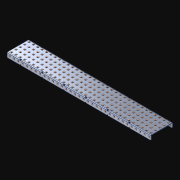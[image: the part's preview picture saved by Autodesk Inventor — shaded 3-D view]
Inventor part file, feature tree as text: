
AUTODESK INVENTOR PART (.ipt)
format: ipt  version: 2021 (Build 250183000, 183)  size: 2,438,656 bytes
history: native  units: in
note: dims shown in document units (in); Inventor stores cm internally (conversion verified against a paired STEP export)
features: extrude x232, other x232, sketch x4, pattern_linear x3
ambient origin geometry x8: Origin, YZ Plane, XZ Plane, XY Plane, X Axis, Y Axis, Z Axis, Center Point
bodies: Solid1 (feature_tree)
feature tree (471):
  pattern_linear  "Rectangular Pattern1"  Spacing1=0.182in  [1 undecoded]
  pattern_linear  "Rectangular Pattern2"  Spacing1=0.046in  [1 undecoded]
  pattern_linear  "Rectangular Pattern3"  Spacing1=0.5in  [1 undecoded]
  extrude  "Extrusion1"  Depth=1.0in
  sketch  "Sketch1"  dims[d0=0.182in]
  other  "Srf1"
  sketch  "Sketch2"  dims[d1=0.046in d2=0.0in]
  other  "Srf2"
  sketch  "Sketch3"  dims[d3=0.182in]
  other  "Srf3"
  other  "Srf4"
  other  "Srf5"
  other  "Srf6"
  other  "Srf7"
  other  "Srf8"
  other  "Srf9"
  other  "Srf10"
  other  "Srf11"
  other  "Srf12"
  other  "Srf13"
  other  "Srf14"
  other  "Srf15"
  other  "Srf16"
  other  "Srf17"
  other  "Srf18"
  other  "Srf19"
  other  "Srf20"
  other  "Srf21"
  other  "Srf22"
  other  "Srf23"
  other  "Srf24"
  other  "Srf25"
  other  "Srf26"
  other  "Srf27"
  other  "Srf28"
  other  "Srf29"
  other  "Srf30"
  other  "Srf31"
  other  "Srf32"
  other  "Srf33"
  other  "Srf34"
  other  "Srf35"
  other  "Srf38"
  other  "Srf39"
  other  "Srf40"
  other  "Srf41"
  other  "Srf42"
  other  "Srf43"
  other  "Srf44"
  other  "Srf45"
  other  "Srf46"
  other  "Srf47"
  other  "Srf48"
  other  "Srf49"
  other  "Srf50"
  other  "Srf51"
  other  "Srf52"
  other  "Srf53"
  other  "Srf54"
  other  "Srf55"
  other  "Srf56"
  other  "Srf57"
  other  "Srf58"
  other  "Srf59"
  other  "Srf60"
  other  "Srf61"
  other  "Srf62"
  other  "Srf63"
  other  "Srf64"
  other  "Srf65"
  other  "Srf66"
  other  "Srf67"
  other  "Srf68"
  other  "Srf69"
  other  "Srf72"
  other  "Srf73"
  other  "Srf74"
  other  "Srf75"
  other  "Srf76"
  other  "Srf77"
  other  "Srf78"
  other  "Srf79"
  other  "Srf80"
  other  "Srf81"
  other  "Srf82"
  other  "Srf83"
  other  "Srf84"
  other  "Srf85"
  other  "Srf86"
  other  "Srf87"
  other  "Srf88"
  other  "Srf89"
  other  "Srf90"
  other  "Srf91"
  other  "Srf92"
  other  "Srf93"
  other  "Srf94"
  other  "Srf95"
  other  "Srf96"
  other  "Srf97"
  other  "Srf98"
  other  "Srf99"
  other  "Srf100"
  other  "Srf101"
  other  "Srf102"
  other  "Srf103"
  other  "Srf104"
  other  "Srf107"
  other  "Srf108"
  other  "Srf109"
  other  "Srf110"
  other  "Srf111"
  other  "Srf112"
  other  "Srf113"
  other  "Srf114"
  other  "Srf115"
  other  "Srf116"
  other  "Srf117"
  other  "Srf118"
  other  "Srf119"
  other  "Srf120"
  other  "Srf121"
  other  "Srf122"
  other  "Srf123"
  other  "Srf124"
  other  "Srf125"
  other  "Srf126"
  other  "Srf127"
  other  "Srf128"
  other  "Srf129"
  other  "Srf130"
  other  "Srf131"
  other  "Srf132"
  other  "Srf133"
  other  "Srf134"
  other  "Srf135"
  other  "Srf136"
  other  "Srf137"
  other  "Srf138"
  other  "Srf139"
  other  "Srf142"
  other  "Srf143"
  other  "Srf144"
  other  "Srf145"
  other  "Srf146"
  other  "Srf147"
  other  "Srf148"
  other  "Srf149"
  other  "Srf150"
  other  "Srf151"
  other  "Srf152"
  other  "Srf153"
  other  "Srf154"
  other  "Srf155"
  other  "Srf156"
  other  "Srf157"
  other  "Srf158"
  other  "Srf159"
  other  "Srf160"
  other  "Srf161"
  other  "Srf162"
  other  "Srf163"
  other  "Srf164"
  other  "Srf165"
  other  "Srf166"
  other  "Srf167"
  other  "Srf168"
  other  "Srf169"
  other  "Srf170"
  other  "Srf171"
  other  "Srf172"
  other  "Srf173"
  other  "Srf174"
  other  "Srf177"
  other  "Srf178"
  other  "Srf179"
  other  "Srf180"
  other  "Srf181"
  other  "Srf182"
  other  "Srf183"
  other  "Srf184"
  other  "Srf185"
  other  "Srf186"
  other  "Srf187"
  other  "Srf188"
  other  "Srf189"
  other  "Srf190"
  other  "Srf191"
  other  "Srf192"
  other  "Srf193"
  other  "Srf194"
  other  "Srf195"
  other  "Srf196"
  other  "Srf197"
  other  "Srf198"
  other  "Srf199"
  other  "Srf200"
  other  "Srf201"
  other  "Srf202"
  other  "Srf203"
  other  "Srf204"
  other  "Srf205"
  other  "Srf206"
  other  "Srf207"
  other  "Srf208"
  other  "Srf209"
  other  "Srf212"
  other  "Srf213"
  other  "Srf214"
  other  "Srf215"
  other  "Srf216"
  other  "Srf217"
  other  "Srf218"
  other  "Srf219"
  other  "Srf220"
  other  "Srf221"
  other  "Srf222"
  other  "Srf223"
  other  "Srf224"
  other  "Srf225"
  other  "Srf226"
  other  "Srf227"
  other  "Srf228"
  other  "Srf229"
  other  "Srf230"
  other  "Srf231"
  other  "Srf232"
  other  "Srf233"
  other  "Srf234"
  other  "Srf235"
  other  "Srf236"
  other  "Srf237"
  other  "Srf238"
  other  "Srf239"
  other  "Srf240"
  other  "Srf241"
  other  "Srf242"
  other  "Srf243"
  sketch  "Sketch4"  dims[d4=0.046in d5=0.0in d6=0.182in d7=0.046in d8=0.0in d11=0.5in d12=12.9921in d14=0.5in d15=1.9685in d17=0.5in d18=12.9921in d20=0.5in d21=1.0in d22=0.0in]
  parser-record x1  (decoder bookkeeping rows leaked as tree rows — omitted from the tree; the rows remain in map.json)
  extrude  "ExtrusionSrf1"  Depth=1.0in
  extrude  "ExtrusionSrf2"  Depth=1.0in
  extrude  "ExtrusionSrf3"  Depth=1.0in
  extrude  "ExtrusionSrf4"  Depth=1.0in
  extrude  "ExtrusionSrf5"  Depth=1.0in
  extrude  "ExtrusionSrf6"  TaperAngle=0.0deg  [1 undecoded]
  extrude  "ExtrusionSrf7"  [1 undecoded]
  extrude  "ExtrusionSrf8"  [1 undecoded]
  extrude  "ExtrusionSrf9"  [1 undecoded]
  extrude  "ExtrusionSrf10"  [1 undecoded]
  extrude  "ExtrusionSrf11"  [1 undecoded]
  extrude  "ExtrusionSrf12"  [1 undecoded]
  extrude  "ExtrusionSrf13"  [1 undecoded]
  extrude  "ExtrusionSrf14"  [1 undecoded]
  extrude  "ExtrusionSrf15"  [1 undecoded]
  extrude  "ExtrusionSrf16"  [1 undecoded]
  extrude  "ExtrusionSrf17"  [1 undecoded]
  extrude  "ExtrusionSrf18"  [1 undecoded]
  extrude  "ExtrusionSrf19"  [1 undecoded]
  extrude  "ExtrusionSrf20"  [1 undecoded]
  extrude  "ExtrusionSrf21"  [1 undecoded]
  extrude  "ExtrusionSrf22"  [1 undecoded]
  extrude  "ExtrusionSrf23"  [1 undecoded]
  extrude  "ExtrusionSrf24"  [1 undecoded]
  extrude  "ExtrusionSrf25"  [1 undecoded]
  extrude  "ExtrusionSrf26"  [1 undecoded]
  extrude  "ExtrusionSrf27"  [1 undecoded]
  extrude  "ExtrusionSrf28"  [1 undecoded]
  extrude  "ExtrusionSrf29"  [1 undecoded]
  extrude  "ExtrusionSrf30"  [1 undecoded]
  extrude  "ExtrusionSrf31"  [1 undecoded]
  extrude  "ExtrusionSrf32"  [1 undecoded]
  extrude  "ExtrusionSrf33"  [1 undecoded]
  extrude  "ExtrusionSrf34"  [1 undecoded]
  extrude  "ExtrusionSrf35"  [1 undecoded]
  extrude  "ExtrusionSrf38"  [1 undecoded]
  extrude  "ExtrusionSrf39"  [1 undecoded]
  extrude  "ExtrusionSrf40"  [1 undecoded]
  extrude  "ExtrusionSrf41"  [1 undecoded]
  extrude  "ExtrusionSrf42"  [1 undecoded]
  extrude  "ExtrusionSrf43"  [1 undecoded]
  extrude  "ExtrusionSrf44"  [1 undecoded]
  extrude  "ExtrusionSrf45"  [1 undecoded]
  extrude  "ExtrusionSrf46"  [1 undecoded]
  extrude  "ExtrusionSrf47"  [1 undecoded]
  extrude  "ExtrusionSrf48"  [1 undecoded]
  extrude  "ExtrusionSrf49"  [1 undecoded]
  extrude  "ExtrusionSrf50"  [1 undecoded]
  extrude  "ExtrusionSrf51"  [1 undecoded]
  extrude  "ExtrusionSrf52"  [1 undecoded]
  extrude  "ExtrusionSrf53"  [1 undecoded]
  extrude  "ExtrusionSrf54"  [1 undecoded]
  extrude  "ExtrusionSrf55"  [1 undecoded]
  extrude  "ExtrusionSrf56"  [1 undecoded]
  extrude  "ExtrusionSrf57"  [1 undecoded]
  extrude  "ExtrusionSrf58"  [1 undecoded]
  extrude  "ExtrusionSrf59"  [1 undecoded]
  extrude  "ExtrusionSrf60"  [1 undecoded]
  extrude  "ExtrusionSrf61"  [1 undecoded]
  extrude  "ExtrusionSrf62"  [1 undecoded]
  extrude  "ExtrusionSrf63"  [1 undecoded]
  extrude  "ExtrusionSrf64"  [1 undecoded]
  extrude  "ExtrusionSrf65"  [1 undecoded]
  extrude  "ExtrusionSrf66"  [1 undecoded]
  extrude  "ExtrusionSrf67"  [1 undecoded]
  extrude  "ExtrusionSrf68"  [1 undecoded]
  extrude  "ExtrusionSrf69"  [1 undecoded]
  extrude  "ExtrusionSrf72"  [1 undecoded]
  extrude  "ExtrusionSrf73"  [1 undecoded]
  extrude  "ExtrusionSrf74"  [1 undecoded]
  extrude  "ExtrusionSrf75"  [1 undecoded]
  extrude  "ExtrusionSrf76"  [1 undecoded]
  extrude  "ExtrusionSrf77"  [1 undecoded]
  extrude  "ExtrusionSrf78"  [1 undecoded]
  extrude  "ExtrusionSrf79"  [1 undecoded]
  extrude  "ExtrusionSrf80"  [1 undecoded]
  extrude  "ExtrusionSrf81"  [1 undecoded]
  extrude  "ExtrusionSrf82"  [1 undecoded]
  extrude  "ExtrusionSrf83"  [1 undecoded]
  extrude  "ExtrusionSrf84"  [1 undecoded]
  extrude  "ExtrusionSrf85"  [1 undecoded]
  extrude  "ExtrusionSrf86"  [1 undecoded]
  extrude  "ExtrusionSrf87"  [1 undecoded]
  extrude  "ExtrusionSrf88"  [1 undecoded]
  extrude  "ExtrusionSrf89"  [1 undecoded]
  extrude  "ExtrusionSrf90"  [1 undecoded]
  extrude  "ExtrusionSrf91"  [1 undecoded]
  extrude  "ExtrusionSrf92"  [1 undecoded]
  extrude  "ExtrusionSrf93"  [1 undecoded]
  extrude  "ExtrusionSrf94"  [1 undecoded]
  extrude  "ExtrusionSrf95"  [1 undecoded]
  extrude  "ExtrusionSrf96"  [1 undecoded]
  extrude  "ExtrusionSrf97"  [1 undecoded]
  extrude  "ExtrusionSrf98"  [1 undecoded]
  extrude  "ExtrusionSrf99"  [1 undecoded]
  extrude  "ExtrusionSrf100"  [1 undecoded]
  extrude  "ExtrusionSrf101"  [1 undecoded]
  extrude  "ExtrusionSrf102"  [1 undecoded]
  extrude  "ExtrusionSrf103"  [1 undecoded]
  extrude  "ExtrusionSrf104"  [1 undecoded]
  extrude  "ExtrusionSrf107"  [1 undecoded]
  extrude  "ExtrusionSrf108"  [1 undecoded]
  extrude  "ExtrusionSrf109"  [1 undecoded]
  extrude  "ExtrusionSrf110"  [1 undecoded]
  extrude  "ExtrusionSrf111"  [1 undecoded]
  extrude  "ExtrusionSrf112"  [1 undecoded]
  extrude  "ExtrusionSrf113"  [1 undecoded]
  extrude  "ExtrusionSrf114"  [1 undecoded]
  extrude  "ExtrusionSrf115"  [1 undecoded]
  extrude  "ExtrusionSrf116"  [1 undecoded]
  extrude  "ExtrusionSrf117"  [1 undecoded]
  extrude  "ExtrusionSrf118"  [1 undecoded]
  extrude  "ExtrusionSrf119"  [1 undecoded]
  extrude  "ExtrusionSrf120"  [1 undecoded]
  extrude  "ExtrusionSrf121"  [1 undecoded]
  extrude  "ExtrusionSrf122"  [1 undecoded]
  extrude  "ExtrusionSrf123"  [1 undecoded]
  extrude  "ExtrusionSrf124"  [1 undecoded]
  extrude  "ExtrusionSrf125"  [1 undecoded]
  extrude  "ExtrusionSrf126"  [1 undecoded]
  extrude  "ExtrusionSrf127"  [1 undecoded]
  extrude  "ExtrusionSrf128"  [1 undecoded]
  extrude  "ExtrusionSrf129"  [1 undecoded]
  extrude  "ExtrusionSrf130"  [1 undecoded]
  extrude  "ExtrusionSrf131"  [1 undecoded]
  extrude  "ExtrusionSrf132"  [1 undecoded]
  extrude  "ExtrusionSrf133"  [1 undecoded]
  extrude  "ExtrusionSrf134"  [1 undecoded]
  extrude  "ExtrusionSrf135"  [1 undecoded]
  extrude  "ExtrusionSrf136"  [1 undecoded]
  extrude  "ExtrusionSrf137"  [1 undecoded]
  extrude  "ExtrusionSrf138"  [1 undecoded]
  extrude  "ExtrusionSrf139"  [1 undecoded]
  extrude  "ExtrusionSrf142"  [1 undecoded]
  extrude  "ExtrusionSrf143"  [1 undecoded]
  extrude  "ExtrusionSrf144"  [1 undecoded]
  extrude  "ExtrusionSrf145"  [1 undecoded]
  extrude  "ExtrusionSrf146"  [1 undecoded]
  extrude  "ExtrusionSrf147"  [1 undecoded]
  extrude  "ExtrusionSrf148"  [1 undecoded]
  extrude  "ExtrusionSrf149"  [1 undecoded]
  extrude  "ExtrusionSrf150"  [1 undecoded]
  extrude  "ExtrusionSrf151"  [1 undecoded]
  extrude  "ExtrusionSrf152"  [1 undecoded]
  extrude  "ExtrusionSrf153"  [1 undecoded]
  extrude  "ExtrusionSrf154"  [1 undecoded]
  extrude  "ExtrusionSrf155"  [1 undecoded]
  extrude  "ExtrusionSrf156"  [1 undecoded]
  extrude  "ExtrusionSrf157"  [1 undecoded]
  extrude  "ExtrusionSrf158"  [1 undecoded]
  extrude  "ExtrusionSrf159"  [1 undecoded]
  extrude  "ExtrusionSrf160"  [1 undecoded]
  extrude  "ExtrusionSrf161"  [1 undecoded]
  extrude  "ExtrusionSrf162"  [1 undecoded]
  extrude  "ExtrusionSrf163"  [1 undecoded]
  extrude  "ExtrusionSrf164"  [1 undecoded]
  extrude  "ExtrusionSrf165"  [1 undecoded]
  extrude  "ExtrusionSrf166"  [1 undecoded]
  extrude  "ExtrusionSrf167"  [1 undecoded]
  extrude  "ExtrusionSrf168"  [1 undecoded]
  extrude  "ExtrusionSrf169"  [1 undecoded]
  extrude  "ExtrusionSrf170"  [1 undecoded]
  extrude  "ExtrusionSrf171"  [1 undecoded]
  extrude  "ExtrusionSrf172"  [1 undecoded]
  extrude  "ExtrusionSrf173"  [1 undecoded]
  extrude  "ExtrusionSrf174"  [1 undecoded]
  extrude  "ExtrusionSrf177"  [1 undecoded]
  extrude  "ExtrusionSrf178"  [1 undecoded]
  extrude  "ExtrusionSrf179"  [1 undecoded]
  extrude  "ExtrusionSrf180"  [1 undecoded]
  extrude  "ExtrusionSrf181"  [1 undecoded]
  extrude  "ExtrusionSrf182"  [1 undecoded]
  extrude  "ExtrusionSrf183"  [1 undecoded]
  extrude  "ExtrusionSrf184"  [1 undecoded]
  extrude  "ExtrusionSrf185"  [1 undecoded]
  extrude  "ExtrusionSrf186"  [1 undecoded]
  extrude  "ExtrusionSrf187"  [1 undecoded]
  extrude  "ExtrusionSrf188"  [1 undecoded]
  extrude  "ExtrusionSrf189"  [1 undecoded]
  extrude  "ExtrusionSrf190"  [1 undecoded]
  extrude  "ExtrusionSrf191"  [1 undecoded]
  extrude  "ExtrusionSrf192"  [1 undecoded]
  extrude  "ExtrusionSrf193"  [1 undecoded]
  extrude  "ExtrusionSrf194"  [1 undecoded]
  extrude  "ExtrusionSrf195"  [1 undecoded]
  extrude  "ExtrusionSrf196"  [1 undecoded]
  extrude  "ExtrusionSrf197"  [1 undecoded]
  extrude  "ExtrusionSrf198"  [1 undecoded]
  extrude  "ExtrusionSrf199"  [1 undecoded]
  extrude  "ExtrusionSrf200"  [1 undecoded]
  extrude  "ExtrusionSrf201"  [1 undecoded]
  extrude  "ExtrusionSrf202"  [1 undecoded]
  extrude  "ExtrusionSrf203"  [1 undecoded]
  extrude  "ExtrusionSrf204"  [1 undecoded]
  extrude  "ExtrusionSrf205"  [1 undecoded]
  extrude  "ExtrusionSrf206"  [1 undecoded]
  extrude  "ExtrusionSrf207"  [1 undecoded]
  extrude  "ExtrusionSrf208"  [1 undecoded]
  extrude  "ExtrusionSrf209"  [1 undecoded]
  extrude  "ExtrusionSrf212"  [1 undecoded]
  extrude  "ExtrusionSrf213"  [1 undecoded]
  extrude  "ExtrusionSrf214"  [1 undecoded]
  extrude  "ExtrusionSrf215"  [1 undecoded]
  extrude  "ExtrusionSrf216"  [1 undecoded]
  extrude  "ExtrusionSrf217"  [1 undecoded]
  extrude  "ExtrusionSrf218"  [1 undecoded]
  extrude  "ExtrusionSrf219"  [1 undecoded]
  extrude  "ExtrusionSrf220"  [1 undecoded]
  extrude  "ExtrusionSrf221"  [1 undecoded]
  extrude  "ExtrusionSrf222"  [1 undecoded]
  extrude  "ExtrusionSrf223"  [1 undecoded]
  extrude  "ExtrusionSrf224"  [1 undecoded]
  extrude  "ExtrusionSrf225"  [1 undecoded]
  extrude  "ExtrusionSrf226"  [1 undecoded]
  extrude  "ExtrusionSrf227"  [1 undecoded]
  extrude  "ExtrusionSrf228"  [1 undecoded]
  extrude  "ExtrusionSrf229"  [1 undecoded]
  extrude  "ExtrusionSrf230"  [1 undecoded]
  extrude  "ExtrusionSrf231"  [1 undecoded]
  extrude  "ExtrusionSrf232"  [1 undecoded]
  extrude  "ExtrusionSrf233"  [1 undecoded]
  extrude  "ExtrusionSrf234"  [1 undecoded]
  extrude  "ExtrusionSrf235"  [1 undecoded]
  extrude  "ExtrusionSrf236"  [1 undecoded]
  extrude  "ExtrusionSrf237"  [1 undecoded]
  extrude  "ExtrusionSrf238"  [1 undecoded]
  extrude  "ExtrusionSrf239"  [1 undecoded]
  extrude  "ExtrusionSrf240"  [1 undecoded]
  extrude  "ExtrusionSrf241"  [1 undecoded]
  extrude  "ExtrusionSrf242"  [1 undecoded]
  extrude  "ExtrusionSrf243"  [1 undecoded]
note: 229 required parameter values undecoded (feature->parameter linkage not recoverable at this tier; creation-order binding heuristic only, values carry confidence <= 0.55)
